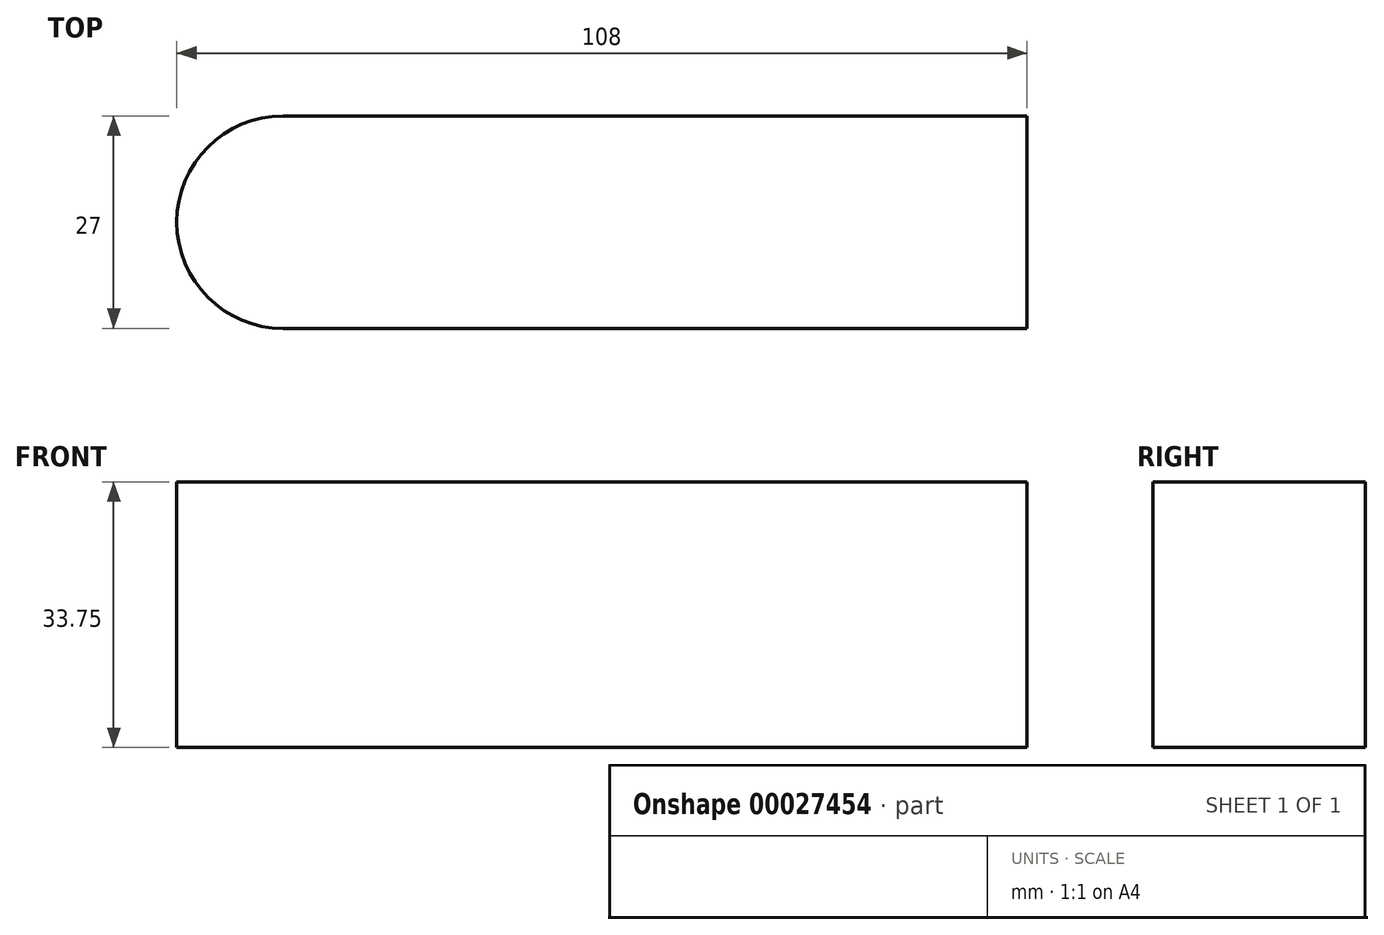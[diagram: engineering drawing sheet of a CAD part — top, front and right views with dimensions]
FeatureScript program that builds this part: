
annotation { "Feature Type Name" : "Feature", "Feature Type Description" : "" }
export const myFeature = defineFeature(function(context is Context, id is Id, definition is map)
    precondition{}
    {
        {
            var Q0;
            Q0=qCreatedBy(makeId("Top.planeOp"),FACE);
            var sketch = newSketch(context, id + "F0", { "sketchPlane" : qUnion([Q0])});
            skLineSegment(sketch, "E0.rect.bottom", {"start": v(-40.5, 13.5) * mm, "end": v(54, 13.5) * mm});
            skLineSegment(sketch, "E0.rect.top", {"start": v(-40.5, -13.5) * mm, "end": v(54, -13.5) * mm});
            skLineSegment(sketch, "E0.rect.left", {"start": v(-54, 0) * mm, "end": v(-54, 0) * mm});
            skLineSegment(sketch, "E0.rect.right", {"start": v(54, 13.5) * mm, "end": v(54, -13.5) * mm});
            skPoint(sketch, "E0.rect.middle", {"position": v(0, 0) * mm});
            skPoint(sketch, "E1.visualSharp", {"position": v(-54, 13.5) * mm});
            skArc(sketch, "E1.filletArc", {"start": v(-40.5, 13.5) * mm, "mid": v(-50.05, 9.55) * mm, "end": v(-54, 0) * mm});
            skPoint(sketch, "E2.visualSharp", {"position": v(-54, -13.5) * mm});
            skArc(sketch, "E2.filletArc", {"start": v(-54, 0) * mm, "mid": v(-50.05, -9.55) * mm, "end": v(-40.5, -13.5) * mm});
            skSolve(sketch);
        }
        {
            var Q0;
            Q0 = qSketchRegion(id + "F0", true);
            extrude(context, id + "F1", {"entities" : qUnion([Q0]), "depth" : 33.75 * mm});
        }
    });
